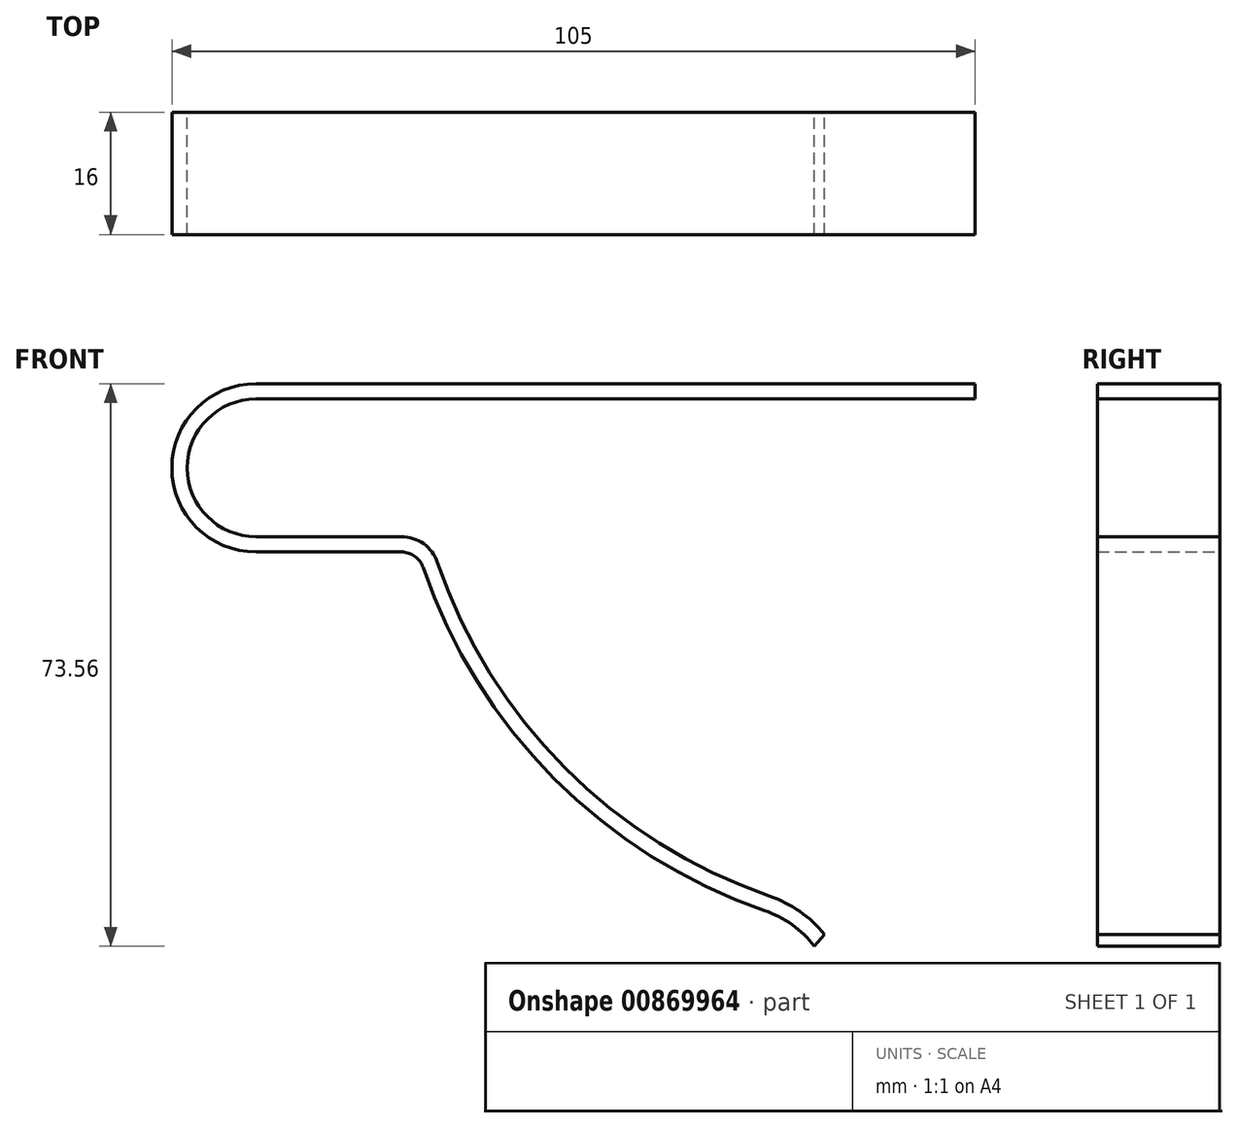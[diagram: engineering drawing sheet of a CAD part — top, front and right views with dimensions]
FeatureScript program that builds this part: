
annotation { "Feature Type Name" : "Feature", "Feature Type Description" : "" }
export const myFeature = defineFeature(function(context is Context, id is Id, definition is map)
    precondition{}
    {
        {
            var Q0;
            Q0=qCreatedBy(makeId("Front.planeOp"),FACE);
            var sketch = newSketch(context, id + "F0", { "sketchPlane" : qUnion([Q0])});
            skArc(sketch, "E0", {"start": v(0, 9) * mm, "mid": v(-9, 0) * mm, "end": v(0, -9) * mm});
            skLineSegment(sketch, "E1", {"start": v(0, 9) * mm, "end": v(94, 9) * mm});
            skLineSegment(sketch, "E2", {"start": v(0, -9) * mm, "end": v(19, -9) * mm});
            skArc(sketch, "E3", {"start": v(23.73, -12.39) * mm, "mid": v(40.4, -39.22) * mm, "end": v(67.15, -56) * mm});
            skArc(sketch, "E4", {"start": v(74.32, -61) * mm, "mid": v(71.08, -58) * mm, "end": v(67.15, -56) * mm});
            skPoint(sketch, "E5.visualSharp", {"position": v(22.67, -9) * mm});
            skArc(sketch, "E5.filletArc", {"start": v(23.73, -12.39) * mm, "mid": v(21.91, -9.93) * mm, "end": v(19, -9) * mm});
            skArc(sketch, "E6.0", {"start": v(73, -62.56) * mm, "mid": v(70.1, -59.75) * mm, "end": v(66.5, -57.9) * mm});
            skLineSegment(sketch, "E6.1", {"start": v(0, 11) * mm, "end": v(94, 11) * mm});
            skArc(sketch, "E6.2", {"start": v(0, 11) * mm, "mid": v(-11, 0) * mm, "end": v(0, -11) * mm});
            skLineSegment(sketch, "E6.3", {"start": v(0, -11) * mm, "end": v(19, -11) * mm});
            skArc(sketch, "E6.4", {"start": v(21.84, -13.03) * mm, "mid": v(38.98, -40.63) * mm, "end": v(66.5, -57.9) * mm});
            skLineSegment(sketch, "E7", {"start": v(94, 11) * mm, "end": v(94, 9) * mm});
            skLineSegment(sketch, "E8", {"start": v(74.32, -61) * mm, "end": v(73, -62.56) * mm});
            skPoint(sketch, "E9.visualSharp", {"position": v(21.18, -11) * mm});
            skArc(sketch, "E9.filletArc", {"start": v(21.84, -13.03) * mm, "mid": v(20.75, -11.56) * mm, "end": v(19, -11) * mm});
            skSolve(sketch);
        }
        {
            var Q0;
            Q0=makeQuery(id+"F0.imprint","IMPRINT",FACE,{"disambiguationData":[TD([[makeQuery(id+"F0.imprint","IMPRINT",EDGE,{"derivedFrom":sQuery(id+"F0.wireOp",EDGE,"E0")}),-1.0]])]});
            extrude(context, id + "F1", {"entities" : qUnion([Q0]), "depth" : 16 * mm, "offsetDistance" : 25 * mm});
        }
    });
